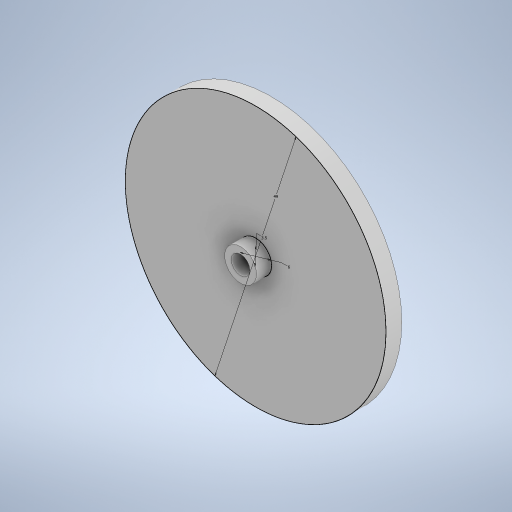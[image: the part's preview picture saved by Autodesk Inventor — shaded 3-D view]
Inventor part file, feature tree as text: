
AUTODESK INVENTOR PART (.ipt)
format: ipt  version: 2023.1 (Build 271208000, 208)  size: 226,304 bytes
history: native  units: mm
features: extrude x2, other x1, sketch x1
ambient origin geometry x8: Origin, YZ Plane, XZ Plane, XY Plane, X Axis, Y Axis, Z Axis, Center Point
bodies: Body1 (feature_tree)
feature tree (4):
  other  "솔리드1"
  sketch  "스케치1"
  extrude  "돌출1"  Depth=49.0mm
  extrude  "돌출2"  Depth=6.0mm
